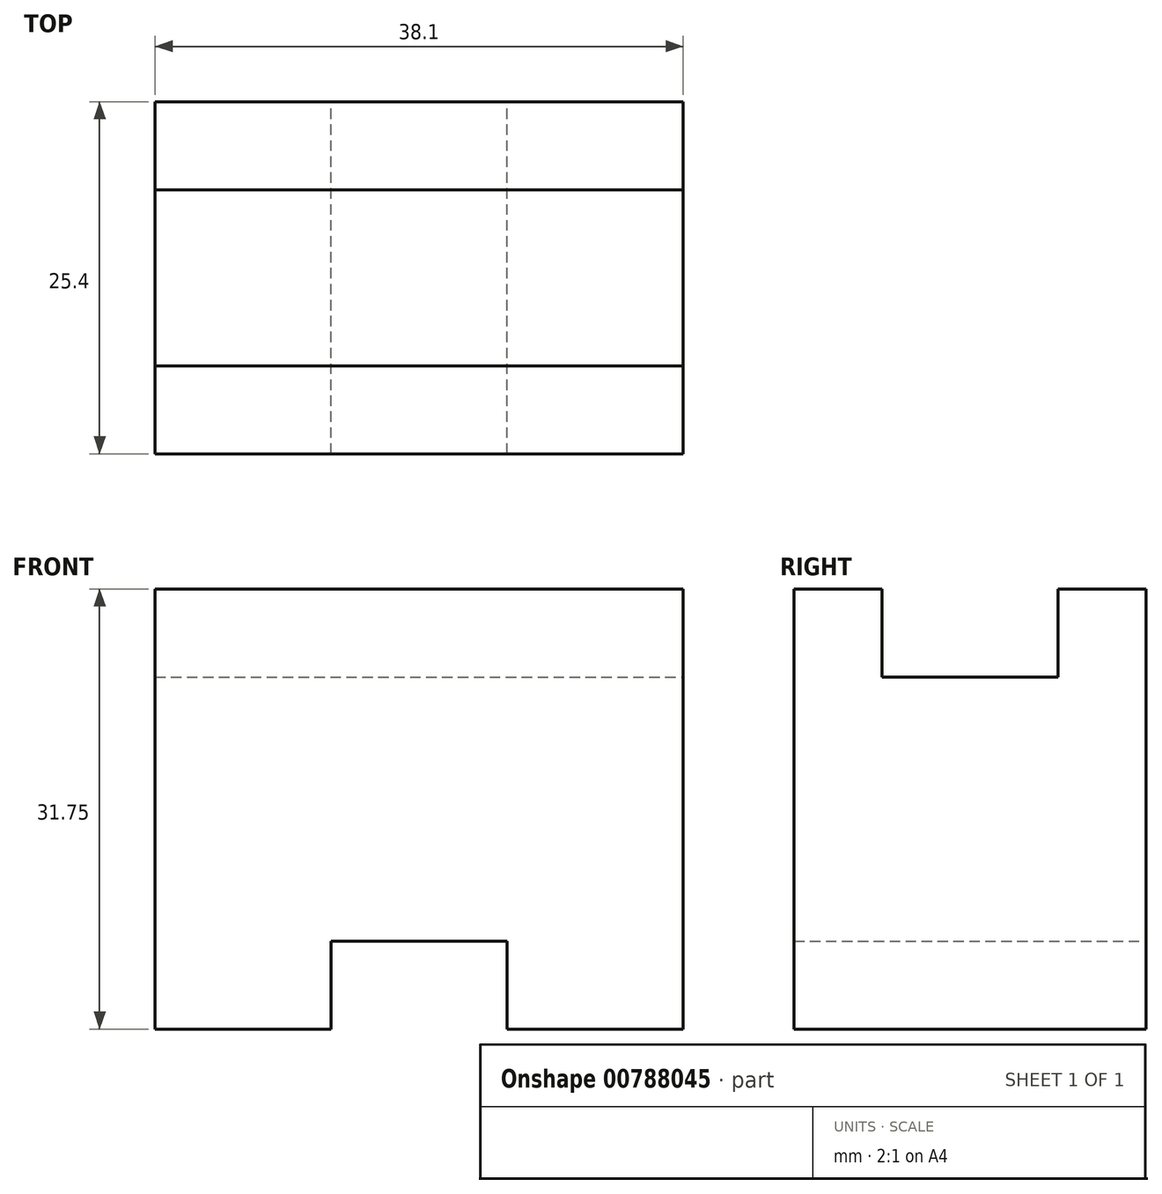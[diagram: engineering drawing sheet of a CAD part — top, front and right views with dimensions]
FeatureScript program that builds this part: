
annotation { "Feature Type Name" : "Feature", "Feature Type Description" : "" }
export const myFeature = defineFeature(function(context is Context, id is Id, definition is map)
    precondition{}
    {
        {
            var Q0;
            Q0=qCreatedBy(makeId("Front.planeOp"),FACE);
            var sketch = newSketch(context, id + "F0", { "sketchPlane" : qUnion([Q0])});
            skLineSegment(sketch, "E0", {"start": v(0, 0) * mm, "end": v(0, 31.75) * mm});
            skLineSegment(sketch, "E1", {"start": v(0, 31.75) * mm, "end": v(38.1, 31.75) * mm});
            skLineSegment(sketch, "E2", {"start": v(38.1, 31.75) * mm, "end": v(38.1, 0) * mm});
            skLineSegment(sketch, "E3", {"start": v(0, 0) * mm, "end": v(12.7, 0) * mm});
            skLineSegment(sketch, "E4", {"start": v(12.7, 0) * mm, "end": v(12.7, 6.35) * mm});
            skLineSegment(sketch, "E5", {"start": v(12.7, 6.35) * mm, "end": v(25.4, 6.35) * mm});
            skLineSegment(sketch, "E6", {"start": v(25.4, 6.35) * mm, "end": v(25.4, 0) * mm});
            skLineSegment(sketch, "E7", {"start": v(25.4, 0) * mm, "end": v(38.1, 0) * mm});
            skSolve(sketch);
        }
        {
            var Q0;
            Q0 = qSketchRegion(id + "F0", true);
            extrude(context, id + "F1", {"entities" : qUnion([Q0]), "depth" : 25.4 * mm, "offsetDistance" : 25.4 * mm});
        }
        {
            var Q0;
            Q0=makeQuery(id+"F1.opExtrude","SWEPT_FACE",FACE,{"disambiguationData":[OSD([sQuery(id+"F0.wireOp",EDGE,"E2")])]});
            var sketch = newSketch(context, id + "F2", { "sketchPlane" : qUnion([Q0])});
            skLineSegment(sketch, "E8", {"start": v(-25.4, 31.75) * mm, "end": v(-19.05, 31.75) * mm, "construction": true});
            skLineSegment(sketch, "E9", {"start": v(0, 31.75) * mm, "end": v(-6.35, 31.75) * mm, "construction": true});
            skLineSegment(sketch, "E10", {"start": v(-6.35, 31.75) * mm, "end": v(-6.35, 25.4) * mm, "construction": true});
            skLineSegment(sketch, "E11", {"start": v(-19.05, 31.75) * mm, "end": v(-19.05, 25.4) * mm, "construction": true});
            skLineSegment(sketch, "E12", {"start": v(-19.05, 31.75) * mm, "end": v(-19.05, 25.4) * mm});
            skLineSegment(sketch, "E13", {"start": v(-6.35, 31.75) * mm, "end": v(-6.35, 25.4) * mm});
            skLineSegment(sketch, "E14", {"start": v(-19.05, 25.4) * mm, "end": v(-6.35, 25.4) * mm});
            skLineSegment(sketch, "E15", {"start": v(-19.05, 31.75) * mm, "end": v(-6.35, 31.75) * mm});
            skSolve(sketch);
        }
        {
            var Q0;
            Q0=makeQuery(id+"F2.imprint","IMPRINT",FACE,{"disambiguationData":[TD([[makeQuery(id+"F2.imprint","IMPRINT",EDGE,{"derivedFrom":sQuery(id+"F2.wireOp",EDGE,"E12")}),1.0]])]});
            extrude(context, id + "F3", {"entities" : qUnion([Q0]), "operationType" : NewBodyOperationType.REMOVE, "oppositeDirection" : true, "depth" : 38.1 * mm, "offsetDistance" : 25.4 * mm});
        }
    });
